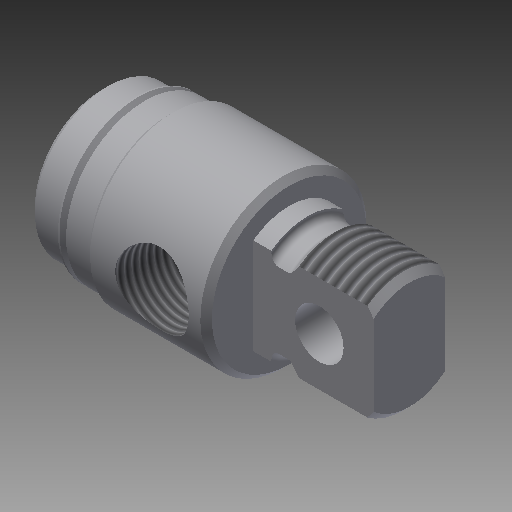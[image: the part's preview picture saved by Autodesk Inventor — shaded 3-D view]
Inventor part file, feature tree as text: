
AUTODESK INVENTOR PART (.ipt)
format: ipt  version: 2019 (Build 230136000, 136)  size: 349,184 bytes
history: native  units: in
note: dims shown in document units (in); Inventor stores cm internally (conversion verified against a paired STEP export)
features: other x154, sketch x7, revolve x4, thread x2, extrude x2, hole x1
ambient origin geometry x8: Origin, YZ Plane, XZ Plane, XY Plane, X Axis, Y Axis, Z Axis, Center Point
bodies: Solid1 (feature_tree)
feature tree (170):
  revolve  "Revolution1"  Angle=360.0deg
  revolve  "Revolution2"  [1 undecoded]
  thread  "Thread1"  [1 undecoded]
  extrude  "Extrusion1"  TaperAngle=360.0deg  [1 undecoded]
  hole  "Hole1"  [1 undecoded]
  revolve  "Revolution3"  [1 undecoded]
  thread  "Thread2"  [1 undecoded]
  revolve  "Revolution4"  [1 undecoded]
  extrude  "Extrusion2"  [1 undecoded]
  other  "1_XY"
  other  "1_YZ"
  other  "1_ZX"
  other  "1_X"
  other  "1_Y"
  other  "1_Z"
  other  "1_Center"
  other  "c1_XY"
  other  "c1_YZ"
  other  "c1_ZX"
  other  "c1_X"
  other  "c1_Y"
  other  "c1_Z"
  other  "c1_Center"
  other  "c2_XY"
  other  "c2_YZ"
  other  "c2_ZX"
  other  "c2_X"
  other  "c2_Y"
  other  "c2_Z"
  other  "c2_Center"
  other  "cc1_XY"
  other  "cc1_YZ"
  other  "cc1_ZX"
  other  "cc1_X"
  other  "cc1_Y"
  other  "cc1_Z"
  other  "cc1_Center"
  other  "cc2_XY"
  other  "cc2_YZ"
  other  "cc2_ZX"
  other  "cc2_X"
  other  "cc2_Y"
  other  "cc2_Z"
  other  "cc2_Center"
  other  "lovra1_XY"
  other  "lovra1_YZ"
  other  "lovra1_ZX"
  other  "lovra1_X"
  other  "lovra1_Y"
  other  "lovra1_Z"
  other  "lovra1_Center"
  other  "lovra2_XY"
  other  "lovra2_YZ"
  other  "lovra2_ZX"
  other  "lovra2_X"
  other  "lovra2_Y"
  other  "lovra2_Z"
  other  "lovra2_Center"
  other  "lovra21_XY"
  other  "lovra21_YZ"
  other  "lovra21_ZX"
  other  "lovra21_X"
  other  "lovra21_Y"
  other  "lovra21_Z"
  other  "lovra21_Center"
  other  "lovra22_XY"
  other  "lovra22_YZ"
  other  "lovra22_ZX"
  other  "lovra22_X"
  other  "lovra22_Y"
  other  "lovra22_Z"
  other  "lovra22_Center"
  other  "lovra3_XY"
  other  "lovra3_YZ"
  other  "lovra3_ZX"
  other  "lovra3_X"
  other  "lovra3_Y"
  other  "lovra3_Z"
  other  "lovra3_Center"
  other  "olen_XY"
  other  "olen_YZ"
  other  "olen_ZX"
  other  "olen_X"
  other  "olen_Y"
  other  "olen_Z"
  other  "olen_Center"
  other  "p1_XY"
  other  "p1_YZ"
  other  "p1_ZX"
  other  "p1_X"
  other  "p1_Y"
  other  "p1_Z"
  other  "p1_Center"
  other  "p2_XY"
  other  "p2_YZ"
  other  "p2_ZX"
  other  "p2_X"
  other  "p2_Y"
  other  "p2_Z"
  other  "p2_Center"
  other  "port_XY"
  other  "port_YZ"
  other  "port_ZX"
  other  "port_X"
  other  "port_Y"
  other  "port_Z"
  other  "port_Center"
  other  "port2_XY"
  other  "port2_YZ"
  other  "port2_ZX"
  other  "port2_X"
  other  "port2_Y"
  other  "port2_Z"
  other  "port2_Center"
  other  "thd1_XY"
  other  "thd1_YZ"
  other  "thd1_ZX"
  other  "thd1_X"
  other  "thd1_Y"
  other  "thd1_Z"
  other  "thd1_Center"
  other  "thd2_XY"
  other  "thd2_YZ"
  other  "thd2_ZX"
  other  "thd2_X"
  other  "thd2_Y"
  other  "thd2_Z"
  other  "thd2_Center"
  other  "to_mounting_bracket_XY"
  other  "to_mounting_bracket_YZ"
  other  "to_mounting_bracket_ZX"
  other  "to_mounting_bracket_X"
  other  "to_mounting_bracket_Y"
  other  "to_mounting_bracket_Z"
  other  "to_mounting_bracket_Center"
  other  "to_nut_XY"
  other  "to_nut_YZ"
  other  "to_nut_ZX"
  other  "to_nut_X"
  other  "to_nut_Y"
  other  "to_nut_Z"
  other  "to_nut_Center"
  other  "to_pin_XY"
  other  "to_pin_YZ"
  other  "to_pin_ZX"
  other  "to_pin_X"
  other  "to_pin_Y"
  other  "to_pin_Z"
  other  "to_pin_Center"
  other  "to_screw_XY"
  other  "to_screw_YZ"
  other  "to_screw_ZX"
  other  "to_screw_X"
  other  "to_screw_Y"
  other  "to_screw_Z"
  other  "to_screw_Center"
  other  "to_tube_XY"
  other  "to_tube_YZ"
  other  "to_tube_ZX"
  other  "to_tube_X"
  other  "to_tube_Y"
  other  "to_tube_Z"
  other  "to_tube_Center"
  sketch  "Sketch_8"  dims[d2=0.3547in d3=0.0in d4=0.625in d5=0.0in]
  sketch  "Sketch_15"  dims[d14=0.3021in d15=0.0in d16=360.0deg]
  sketch  "Sketch_9"  dims[d6=0.312in d7=0.75in d8=0.375in d9=0.25in d10=0.5635in d11=0.9284in d12=120.0deg d13=360.0deg]
  sketch  "Sketch4"  dims[d0=360.0deg d1=360.0deg]
  sketch  "Sketch_68"
  sketch  "Sketch_24"  dims[d17=0.5587in d18=0.0in]
  sketch  "Sketch_43"  dims[d19=0.0in d20=0.0in d21=0.0in d22=0.0in d23=0.0in d24=0.0in d25=0.0in d26=0.0in]
note: 8 required parameter values undecoded (feature->parameter linkage not recoverable at this tier; creation-order binding heuristic only, values carry confidence <= 0.55)